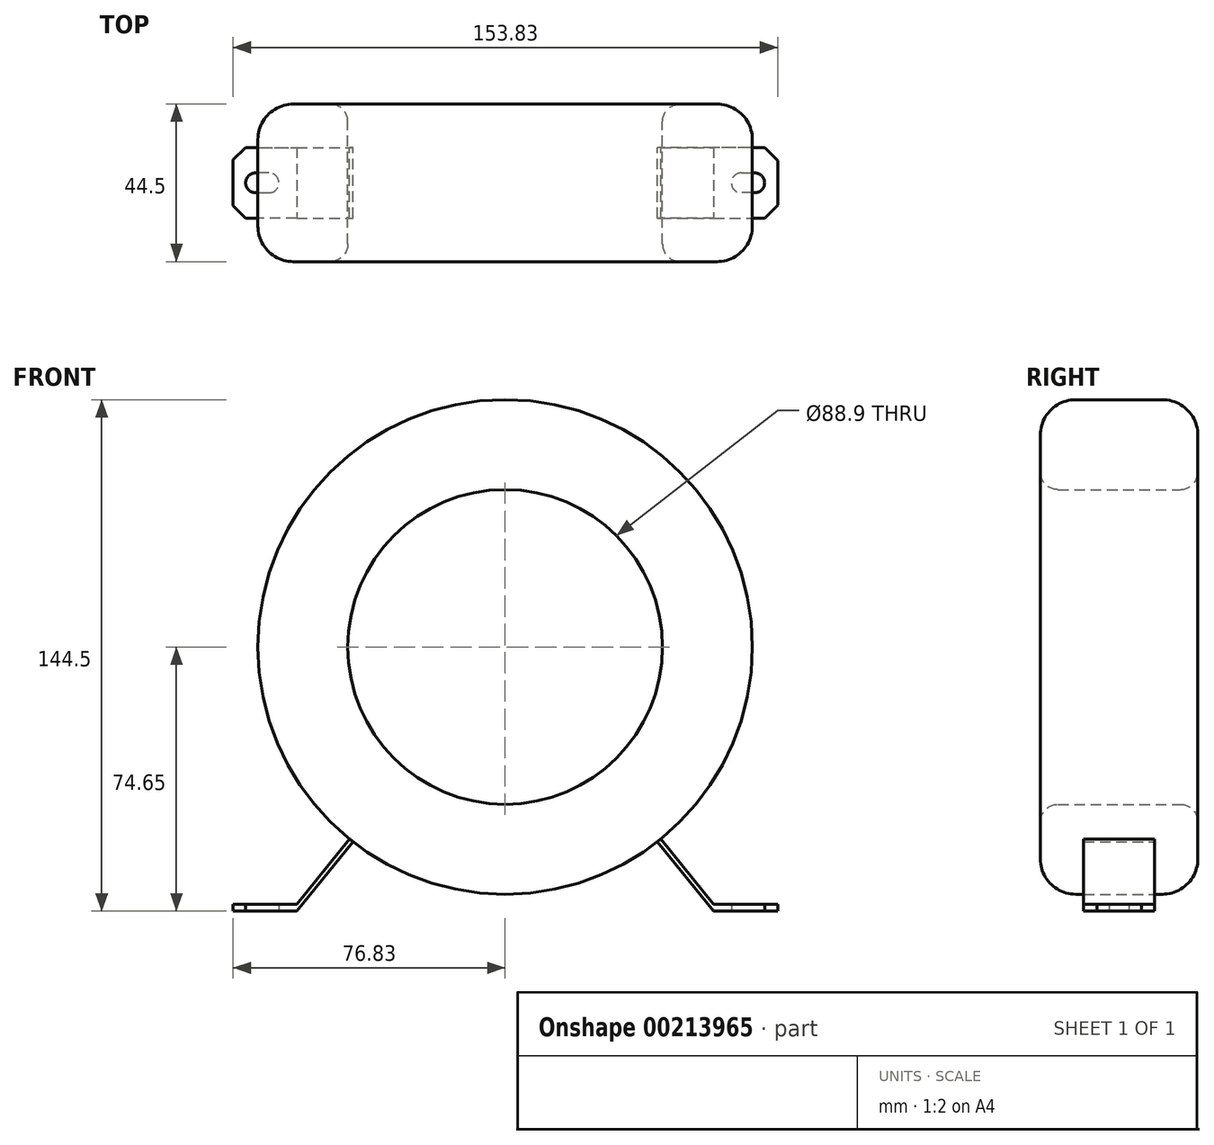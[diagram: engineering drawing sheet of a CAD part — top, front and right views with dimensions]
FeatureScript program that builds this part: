
annotation { "Feature Type Name" : "Feature", "Feature Type Description" : "" }
export const myFeature = defineFeature(function(context is Context, id is Id, definition is map)
    precondition{}
    {
        {
            var Q0;
            Q0=qCreatedBy(makeId("Front.planeOp"),FACE);
            var sketch = newSketch(context, id + "F0", { "sketchPlane" : qUnion([Q0])});
            skCircle(sketch, "E0", {"center": v(0, 69.85) * mm, "radius": 44.45 * mm});
            skCircle(sketch, "E1", {"center": v(0, 69.85) * mm, "radius": 69.85 * mm});
            skPoint(sketch, "E2", {"position": v(0, 0) * mm});
            skPoint(sketch, "E3", {"position": v(0, 25.4) * mm});
            skLineSegment(sketch, "E4", {"start": v(-76.83, -4.8) * mm, "end": v(67.55, -4.8) * mm});
            skSolve(sketch);
        }
        {
            var Q0;
            Q0=makeQuery(id+"F0.imprint","IMPRINT",FACE,{"disambiguationData":[TD([[makeQuery(id+"F0.imprint","IMPRINT",EDGE,{"derivedFrom":sQuery(id+"F0.wireOp",EDGE,"E0")}),-1.0]])]});
            extrude(context, id + "F1", {"entities" : qUnion([Q0]), "endBound" : BoundingType.SYMMETRIC, "depth" : 44.5 * mm});
        }
        {
            var Q0;
            Q0=makeQuery(id+"F1.opExtrude","CAP_EDGE",EDGE,{"disambiguationData":[OSD([sQuery(id+"F0.wireOp",EDGE,"E1")])],"isStart":false});
            var Q1;
            Q1=makeQuery(id+"F1.opExtrude","CAP_EDGE",EDGE,{"disambiguationData":[OSD([sQuery(id+"F0.wireOp",EDGE,"E1")])],"isStart":true});
            fillet(context, id + "F2", {"entities" : qUnion([Q0, Q1]), "radius" : 10 * mm, "tangentPropagation" : true, "allowEdgeOverflow" : false});
        }
        {
            var Q0;
            Q0=makeQuery(id+"F1.opExtrude","CAP_EDGE",EDGE,{"disambiguationData":[OSD([sQuery(id+"F0.wireOp",EDGE,"E0")])],"isStart":true});
            var Q1;
            Q1=makeQuery(id+"F1.opExtrude","CAP_EDGE",EDGE,{"disambiguationData":[OSD([sQuery(id+"F0.wireOp",EDGE,"E0")])],"isStart":false});
            fillet(context, id + "F3", {"entities" : qUnion([Q0, Q1]), "radius" : 5 * mm, "tangentPropagation" : true, "allowEdgeOverflow" : false});
        }
        {
            var Q0;
            Q0=sQuery(id+"F0.wireOp",EDGE,"E4");
            extrude(context, id + "F4", {"bodyType" : ToolBodyType.SURFACE, "surfaceEntities" : qUnion([Q0]), "endBound" : BoundingType.SYMMETRIC, "depth" : 25 * mm});
        }
        {
            var Q0;
            Q0=makeQuery(id+"F4.opExtrude","SWEPT_FACE",FACE,{"disambiguationData":[OSD([sQuery(id+"F0.wireOp",EDGE,"E4")])]});
            var sketch = newSketch(context, id + "F5", { "sketchPlane" : qUnion([Q0])});
            skLineSegment(sketch, "E5", {"start": v(0, -24.95) * mm, "end": v(0, 24.95) * mm, "construction": true});
            skLineSegment(sketch, "E6", {"start": v(-73.3, 0) * mm, "end": v(73.3, 0) * mm, "construction": true});
            skLineSegment(sketch, "E7", {"start": v(58.9, -10) * mm, "end": v(58.9, 10) * mm});
            skLineSegment(sketch, "E8", {"start": v(58.9, 10) * mm, "end": v(73.3, 10) * mm});
            skLineSegment(sketch, "E9", {"start": v(73.3, 10) * mm, "end": v(77, 6.3) * mm});
            skLineSegment(sketch, "E10", {"start": v(77, 6.3) * mm, "end": v(77, -6.3) * mm});
            skLineSegment(sketch, "E11", {"start": v(77, -6.3) * mm, "end": v(73.3, -10) * mm});
            skLineSegment(sketch, "E12", {"start": v(73.3, -10) * mm, "end": v(58.9, -10) * mm});
            skCircle(sketch, "E13", {"center": v(70.5, 0) * mm, "radius": 2.8 * mm});
            skCircle(sketch, "E14", {"center": v(66.7, 0) * mm, "radius": 2.8 * mm});
            skLineSegment(sketch, "E15", {"start": v(66.7, -2.8) * mm, "end": v(70.5, -2.8) * mm});
            skLineSegment(sketch, "E16", {"start": v(70.5, 2.8) * mm, "end": v(66.7, 2.8) * mm});
            skLineSegment(sketch, "E17.MirrorCS", {"start": v(-58.9, -10) * mm, "end": v(-58.9, 10) * mm});
            skLineSegment(sketch, "E18.MirrorCS", {"start": v(-73.3, -10) * mm, "end": v(-58.9, -10) * mm});
            skLineSegment(sketch, "E19.MirrorCS", {"start": v(-77, -6.3) * mm, "end": v(-73.3, -10) * mm});
            skLineSegment(sketch, "E20.MirrorCS", {"start": v(-77, 6.3) * mm, "end": v(-77, -6.3) * mm});
            skLineSegment(sketch, "E21.MirrorCS", {"start": v(-73.3, 10) * mm, "end": v(-77, 6.3) * mm});
            skLineSegment(sketch, "E22.MirrorCS", {"start": v(-58.9, 10) * mm, "end": v(-73.3, 10) * mm});
            skCircle(sketch, "E23.MirrorC", {"center": v(-70.5, 0) * mm, "radius": 2.8 * mm});
            skCircle(sketch, "E24.MirrorC", {"center": v(-66.7, 0) * mm, "radius": 2.8 * mm});
            skLineSegment(sketch, "E25.MirrorCS", {"start": v(-70.5, 2.8) * mm, "end": v(-66.7, 2.8) * mm});
            skLineSegment(sketch, "E26.MirrorCS", {"start": v(-66.7, -2.8) * mm, "end": v(-70.5, -2.8) * mm});
            skSolve(sketch);
        }
        {
            var Q0;
            Q0=makeQuery(id+"F4.opExtrude","SWEPT_BODY",BODY,{"disambiguationData":[OSD([sQuery(id+"F0.wireOp",EDGE,"E4")])]});
            deleteBodies(context, id + "F6", {"entities" : qUnion([Q0])});
        }
        {
            var Q0;
            Q0=makeQuery(id+"F5.imprint","IMPRINT",FACE,{"disambiguationData":[TD([[makeQuery(id+"F5.imprint","IMPRINT",EDGE,{"derivedFrom":sQuery(id+"F5.wireOp",EDGE,"E7")}),-1.0]])]});
            var Q1;
            Q1=makeQuery(id+"F5.imprint","IMPRINT",FACE,{"disambiguationData":[TD([[makeQuery(id+"F5.imprint","IMPRINT",EDGE,{"derivedFrom":sQuery(id+"F5.wireOp",EDGE,"E17.MirrorCS")}),1.0]])]});
            var Q2;
            {var subQ11=sQuery(id+"F5.wireOp",EDGE,"E9");Q2=makeQuery(id+"F5.imprint","IMPRINT",FACE,{"disambiguationData":[TD([[makeQuery(id+"F5.imprint","IMPRINT",EDGE,{"derivedFrom":subQ11}),-1.0]])]});}
            extrude(context, id + "F7", {"entities" : qUnion([Q0, Q1, Q2]), "oppositeDirection" : true, "depth" : 2 * mm});
        }
        {
            var Q0;
            Q0=makeQuery(id+"F7.opExtrude","SWEPT_FACE",FACE,{"disambiguationData":[OSD([sQuery(id+"F5.wireOp",EDGE,"E12")])]});
            var sketch = newSketch(context, id + "F8", { "sketchPlane" : qUnion([Q0])});
            skCircle(sketch, "E27.0", {"center": v(0, 69.85) * mm, "radius": 69.85 * mm});
            skLineSegment(sketch, "E28", {"start": v(-43.99, 15.6) * mm, "end": v(-58.9, -2.8) * mm});
            skLineSegment(sketch, "E29", {"start": v(-58.9, -4.8) * mm, "end": v(-43, 14.8) * mm});
            skPoint(sketch, "E30.0", {"position": v(58.9, -2.8) * mm});
            skPoint(sketch, "E30.1", {"position": v(58.9, -4.8) * mm});
            skLineSegment(sketch, "E31", {"start": v(58.9, -2.8) * mm, "end": v(43.99, 15.6) * mm});
            skLineSegment(sketch, "E32", {"start": v(58.9, -4.8) * mm, "end": v(43, 14.8) * mm});
            skLineSegment(sketch, "E33.0", {"start": v(58.9, -2.8) * mm, "end": v(58.9, -4.8) * mm});
            skSolve(sketch);
        }
        {
            var Q0;
            {var subQ0=sQuery(id+"F8.wireOp",EDGE,"E31");Q0=makeQuery(id+"F8.imprint","IMPRINT",FACE,{"disambiguationData":[TD([[makeQuery(id+"F8.imprint","IMPRINT",EDGE,{"derivedFrom":subQ0}),1.0]])]});}
            var Q1;
            {var subQ0=sQuery(id+"F8.wireOp",EDGE,"E28");Q1=makeQuery(id+"F8.imprint","IMPRINT",FACE,{"disambiguationData":[TD([[makeQuery(id+"F8.imprint","IMPRINT",EDGE,{"derivedFrom":subQ0}),1.0]])]});}
            var Q2;
            Q2=makeQuery(id+"F7.opExtrude","SWEPT_FACE",FACE,{"disambiguationData":[OSD([sQuery(id+"F5.wireOp",EDGE,"E22.MirrorCS")])]});
            extrude(context, id + "F9", {"entities" : qUnion([Q0, Q1]), "operationType" : NewBodyOperationType.ADD, "endBound" : BoundingType.UP_TO_SURFACE, "oppositeDirection" : true, "endBoundEntityFace" : qUnion([Q2]), "depth" : 25 * mm});
        }
    });
